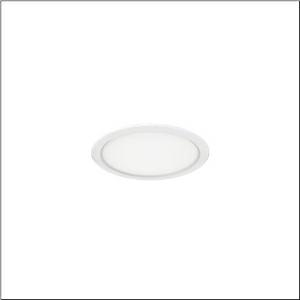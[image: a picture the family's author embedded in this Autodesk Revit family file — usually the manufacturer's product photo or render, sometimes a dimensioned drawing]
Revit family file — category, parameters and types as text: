
# Revit family: lunis_41_eco_51ds107d43b
name_source: partatom
category: Lighting Fixtures
units: mm (PartAtom-declared; Revit-internal decimal feet)

## family parameters
Cut with Voids When Loaded = No
Host = Face
Light Source = No
Part Type = Normal
Room Calculation Point = No
Round Connector Dimension = Use Diameter
Shared = No

## types (1)
- Lunis 41 Eco (1 x LED, 1580 lm, 12 W, 4000K)
    Apparent Load = 12 VA
    CIE Flux Codes = 47 80 97 100 100
    Color Rendering = 80
    Color Temperature = 4000K
    Default Elevation = 1800 mm
    Description = Lunis 41,  Eco, downlight, light emission: direct distribution, LED rated luminous flux: 1.580lm, light colour: 840, mains connection: 230V, AC, 50/60Hz, housing, round, of aluminium, coated, traffic white (RAL 9016), diameter: 166mm, recess depth: 54mm, protection rating (complete): IP20, protection rating (on room side): IP40, insulation class (complete): insulation class II (safety insulation), certification: CE, permissible ambient temperature for indoor applications: -20..+40°C, packaging unit: 1 piece
    Height = 0 mm  [stored 0 ft]
    Lamp = 1 x LED
    Lamp Light Flux = 1580 lm
    Lamp Power = 12 W
    Lamp count = 1
    Length = 166 mm
    Luminous efficacy = 132 lm/W
    Manufacturer = Siteco
    ModVariant = No
    Model = 51DS107D43B
    Mounting Place = Ceiling
    Mounting Type = Recessed
    Number of Poles = 1
    OnlyDefault = Yes
    Power Factor = 1
    Product Name = Lunis 41 Eco
    Product group = downlight
    ProductGroupID = 401
    Protection Class = Protection class II
    Protection Degree = IP 20
    RLX_Detail_Level = 1
    RLX_Emergency_Light_Flux = 0 lm
    RLX_Emergency_Type = 0
    RLX_Emergency_Type_DB = No
    RlxData = <blob elided: 8901 chars, md5=49ab4901>
    Socket = socket
    Standby Power = 0 W
    System Light Flux = 1580 lm
    System Power = 12 W
    Type Comments = Product without accessories
    Type Image = l_1345912.jpg
    URL = http://relux.com
    VarID = ---
    Voltage = 0 V
    Weight = 0.00 kg
    Width = 0 mm  [stored 0 ft]

note: [stored X ft] marks values corroborated as IEEE doubles in the binary element streams (Revit-internal decimal feet)

## geometry (parser evidence)
native form markers: Sweep x8
no freeform markers — native parametric forms only
